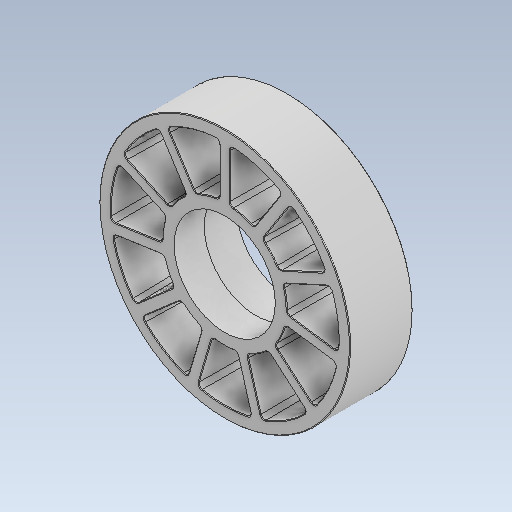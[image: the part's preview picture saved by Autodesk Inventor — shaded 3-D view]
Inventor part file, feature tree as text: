
AUTODESK INVENTOR PART (.ipt)
format: ipt  version: 2020 (Build 240168000, 168)  size: 946,688 bytes
history: native  units: in
note: dims shown in document units (in); Inventor stores cm internally (conversion verified against a paired STEP export)
features: fillet x1
ambient origin geometry x8: Origin, YZ Plane, XZ Plane, XY Plane, X Axis, Y Axis, Z Axis, Center Point
bodies: Solid1 (feature_tree)
feature tree (1):
  fillet  "Fillet2"  [1 undecoded]
note: 1 required parameter value undecoded (feature->parameter linkage not recoverable at this tier; creation-order binding heuristic only, values carry confidence <= 0.55)
